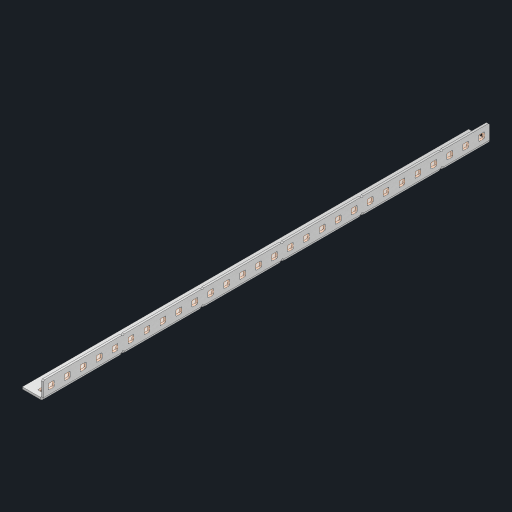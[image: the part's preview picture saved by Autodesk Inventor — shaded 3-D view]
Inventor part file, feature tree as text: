
AUTODESK INVENTOR PART (.ipt)
format: ipt  version: 2023 (Build 270158000, 158)  size: 924,160 bytes
history: native  units: in
note: dims shown in document units (in); Inventor stores cm internally (conversion verified against a paired STEP export)
features: other x61, extrude x55, sheet_metal_op x10, sketch x8, mirror x1, pattern_linear x1, chamfer x1
ambient origin geometry x8: Origin, YZ Plane, XZ Plane, XY Plane, X Axis, Y Axis, Z Axis, Center Point
bodies: Solid1 (feature_tree), Body (feature_tree)
feature tree (137):
  other  "Flange Pattern Plane"
  sheet_metal_op  "Flange Pattern"
  sheet_metal_op  "Body Pattern"
  other  "Arc Length"
  mirror  "Notch Mirror"
  pattern_linear  "Notch Pattern"  Spacing1=0.25in  [1 undecoded]
  chamfer  "End Chamfer"
  extrude  "Half Cut"  Depth=0.0625in
  sketch  "Sketch1"  dims[d0=1.5in]
  other  "Plate1"
  sketch  "Sketch2"  dims[d1=14.0in]
  other  "Plate2"
  sheet_metal_op  "Bend1"
  sheet_metal_op  "Corner1"
  sketch  "Sketch3"  dims[d2=0.0625in]
  other  "Flange Pattern Sketch"
  sketch  "Sketch7"  dims[d3=0.0625in]
  other  "Srf1"
  other  "Srf2"
  sketch  "Sketch8"  dims[d4=0.0312in]
  sketch  "Sketch9"  dims[d5=0.125in]
  other  "Srf91"
  sheet_metal_op  "Body Pattern Sketch"
  other  "Srf92"
  sketch  "Sketch13"  dims[d6=0.0625in]
  sketch  "Sketch14"  dims[d7=0.5in d8=90.0deg d9=0.0312in d10=0.25in d11=0.0625in d12=0.0625in d16=0.182in d17=0.02in d18=0.0625in d19=0.0in d20=0.25in d21=0.25in d46=0.172in d47=1.0in d48=0.0in d49=0.182in d50=0.02in d51=0.25in d52=0.25in d53=0.0625in d54=0.0in d55=0.172in d56=1.0in d57=0.0in d60=11.0236in d62=0.5in d63=0.3937in d65=0.5in d85=0.1473in d86=0.1782in d88=0.04in d89=0.0625in d90=0.0in d91=0.04in d92=0.0491in d95=2.5in d96=0.04in d97=0.25in d98=45.0deg d101=0.0in d102=2.497in d131=0.5in d132=11.0236in d134=0.5in d139=0.5in]
  other  "Srf856"
  other  "Srf1310"
  other  "Srf1311"
  other  "Srf1312"
  other  "Srf1376"
  other  "Srf1377"
  other  "Srf1728"
  other  "Srf1755"
  other  "Srf1878"
  other  "Srf1879"
  other  "Srf1880"
  other  "Srf1881"
  other  "Srf1882"
  other  "Srf1883"
  other  "Srf1884"
  other  "Srf1885"
  other  "Srf1886"
  other  "Srf1887"
  other  "Srf1888"
  other  "Srf1889"
  other  "Srf1890"
  other  "Srf1891"
  other  "Srf1892"
  other  "Srf1893"
  other  "Srf1894"
  other  "Srf1895"
  other  "Srf1896"
  other  "Srf1897"
  other  "Srf1898"
  other  "Srf1899"
  other  "Srf1942"
  other  "Srf1943"
  other  "Srf1944"
  other  "Srf1945"
  other  "Srf1946"
  other  "Srf1947"
  other  "Srf1948"
  other  "Srf1949"
  other  "Srf1950"
  other  "Srf1951"
  other  "Srf1952"
  other  "Srf1953"
  other  "Srf1954"
  other  "Srf1955"
  other  "Srf1956"
  other  "Srf1957"
  other  "Srf1958"
  other  "Srf1959"
  other  "Srf1960"
  other  "Srf1961"
  other  "Srf1962"
  other  "Srf1963"
  sheet_metal_op  "Flange Stamp"
  sheet_metal_op  "Flange Circle"
  sheet_metal_op  "Body Stamp"
  sheet_metal_op  "Body Circle"
  sheet_metal_op  "Notch"
  extrude  "ExtrusionSrf2"  Depth=0.0625in
  extrude  "ExtrusionSrf92"  Depth=0.5in
  extrude  "ExtrusionSrf856"  Depth=0.02in
  extrude  "ExtrusionSrf1310"  Depth=0.0625in
  extrude  "ExtrusionSrf1311"  TaperAngle=0.0deg  [1 undecoded]
  extrude  "ExtrusionSrf1312"  Depth=0.5in
  extrude  "ExtrusionSrf1376"  Depth=0.5in
  extrude  "ExtrusionSrf1377"  Depth=0.5in
  extrude  "ExtrusionSrf1728"  Depth=0.5in TaperAngle=0.0deg
  extrude  "ExtrusionSrf1755"  Depth=0.5in
  extrude  "ExtrusionSrf1878"  Depth=0.02in
  extrude  "ExtrusionSrf1879"  Depth=0.5in
  extrude  "ExtrusionSrf1880"  Depth=0.5in
  extrude  "ExtrusionSrf1881"  Depth=0.0625in
  extrude  "ExtrusionSrf1882"  TaperAngle=0.0deg  [1 undecoded]
  extrude  "ExtrusionSrf1883"  Depth=0.5in
  extrude  "ExtrusionSrf1884"  Depth=0.5in TaperAngle=0.0deg
  extrude  "ExtrusionSrf1885"  Depth=0.5in
  extrude  "ExtrusionSrf1886"  Depth=0.5in
  extrude  "ExtrusionSrf1887"  Depth=0.5in
  extrude  "ExtrusionSrf1888"  Depth=0.5in
  extrude  "ExtrusionSrf1889"  Depth=0.5in
  extrude  "ExtrusionSrf1890"  Depth=0.0625in
  extrude  "ExtrusionSrf1891"  TaperAngle=0.0deg  [1 undecoded]
  extrude  "ExtrusionSrf1892"  Depth=0.5in
  extrude  "ExtrusionSrf1893"  Depth=0.5in
  extrude  "ExtrusionSrf1894"  Depth=0.5in
  extrude  "ExtrusionSrf1895"  Depth=0.5in TaperAngle=45.0deg
  extrude  "ExtrusionSrf1896"  TaperAngle=0.0deg  [1 undecoded]
  extrude  "ExtrusionSrf1897"  Depth=0.5in
  extrude  "ExtrusionSrf1898"  Depth=0.5in
  extrude  "ExtrusionSrf1899"  Depth=0.5in
  extrude  "ExtrusionSrf1942"  Depth=0.5in
  extrude  "ExtrusionSrf1943"  Depth=0.5in
  extrude  "ExtrusionSrf1944"  [1 undecoded]
  extrude  "ExtrusionSrf1945"  [1 undecoded]
  extrude  "ExtrusionSrf1946"  [1 undecoded]
  extrude  "ExtrusionSrf1947"  [1 undecoded]
  extrude  "ExtrusionSrf1948"  [1 undecoded]
  extrude  "ExtrusionSrf1949"  [1 undecoded]
  extrude  "ExtrusionSrf1950"  [1 undecoded]
  extrude  "ExtrusionSrf1951"  [1 undecoded]
  extrude  "ExtrusionSrf1952"  [1 undecoded]
  extrude  "ExtrusionSrf1953"  [1 undecoded]
  extrude  "ExtrusionSrf1954"  [1 undecoded]
  extrude  "ExtrusionSrf1955"  [1 undecoded]
  extrude  "ExtrusionSrf1956"  [1 undecoded]
  extrude  "ExtrusionSrf1957"  [1 undecoded]
  extrude  "ExtrusionSrf1958"  [1 undecoded]
  extrude  "ExtrusionSrf1959"  [1 undecoded]
  extrude  "ExtrusionSrf1960"  [1 undecoded]
  extrude  "ExtrusionSrf1961"  [1 undecoded]
  extrude  "ExtrusionSrf1962"  [1 undecoded]
  extrude  "ExtrusionSrf1963"  [1 undecoded]
note: 25 required parameter values undecoded (feature->parameter linkage not recoverable at this tier; creation-order binding heuristic only, values carry confidence <= 0.55)
